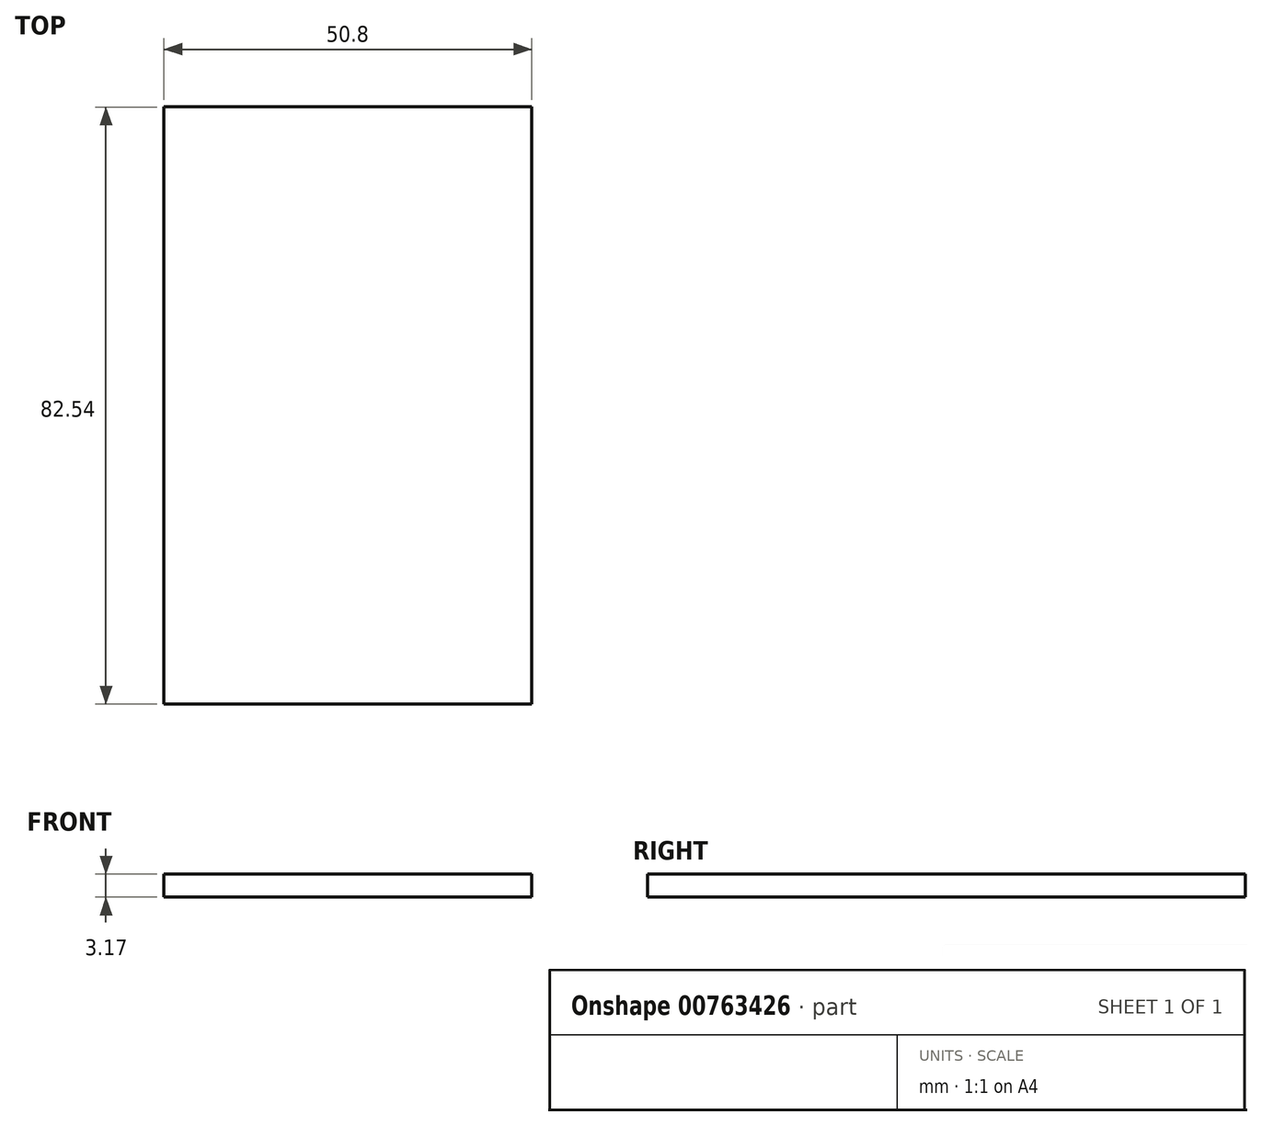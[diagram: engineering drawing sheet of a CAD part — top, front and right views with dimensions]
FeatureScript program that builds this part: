
annotation { "Feature Type Name" : "Feature", "Feature Type Description" : "" }
export const myFeature = defineFeature(function(context is Context, id is Id, definition is map)
    precondition{}
    {
        {
            var Q0;
            Q0=qCreatedBy(makeId("Top.planeOp"),FACE);
            var sketch = newSketch(context, id + "F0", { "sketchPlane" : qUnion([Q0])});
            skLineSegment(sketch, "E0.bottom", {"start": v(-25.4, 41.28) * mm, "end": v(25.4, 41.28) * mm});
            skLineSegment(sketch, "E0.top", {"start": v(-25.4, -41.28) * mm, "end": v(25.4, -41.28) * mm});
            skLineSegment(sketch, "E0.left", {"start": v(-25.4, 41.28) * mm, "end": v(-25.4, -41.28) * mm});
            skLineSegment(sketch, "E0.right", {"start": v(25.4, 41.28) * mm, "end": v(25.4, -41.28) * mm});
            skPoint(sketch, "E0.middle", {"position": v(0, 0) * mm});
            skSolve(sketch);
        }
        {
            var Q0;
            Q0=qCreatedBy(makeId("Top.planeOp"),FACE);
            var sketch = newSketch(context, id + "F1", { "sketchPlane" : qUnion([Q0])});
            skPoint(sketch, "E1", {"position": v(0, -22.23) * mm});
            skSolve(sketch);
        }
        {
            var Q0;
            Q0=qCreatedBy(makeId("Top.planeOp"),FACE);
            var sketch = newSketch(context, id + "F2", { "sketchPlane" : qUnion([Q0])});
            skSolve(sketch);
        }
        {
            var Q0;
            Q0 = qSketchRegion(id + "F2", true);
            var Q1;
            Q1=makeQuery(id+"F0.imprint","IMPRINT",FACE,{"disambiguationData":[TD([[makeQuery(id+"F0.imprint","IMPRINT",EDGE,{"derivedFrom":sQuery(id+"F0.wireOp",EDGE,"E0.bottom")}),-1.0]])]});
            extrude(context, id + "F3", {"entities" : qUnion([Q0, Q1]), "depth" : -3.17 * mm, "offsetDistance" : 25.4 * mm});
        }
        {
            var Q0;
            Q0=sQuery(id+"F1.wireOp",VERTEX,"E1");
            var Q1;
            Q1=makeQuery(id+"F3.opExtrude","SWEPT_BODY",BODY,{"disambiguationData":[OSD([sQuery(id+"F0.wireOp",EDGE,"E0.bottom"),sQuery(id+"F0.wireOp",EDGE,"E0.top"),sQuery(id+"F0.wireOp",EDGE,"E0.left"),sQuery(id+"F0.wireOp",EDGE,"E0.right")])]});
            hole(context, id + "F4", {"style" : HoleStyle.SIMPLE, "endStyle" : HoleEndStyle.THROUGH, "standardTappedOrClearance" : lookupTablePath({ "standard" : "ANSI", "fit" : "Normal (ASME)", "size" : "1", "type" : "Clearance" }), "standardBlindInLast" : lookupTablePath({ "fit" : "Free", "standard" : "ANSI", "size" : "1", "type" : "Clearance" }), "holeDiameter" : 26.2 * mm, "majorDiameter" : 15.88 * mm, "isTappedThrough" : true, "tappedDepth" : 12.7 * mm, "tapClearance" : 3, "locations" : qUnion([Q0]), "scope" : qUnion([Q1])});
        }
        {
            var Q0;
            Q0=makeQuery(id+"F3.opExtrude","SWEPT_FACE",FACE,{"disambiguationData":[OSD([sQuery(id+"F0.wireOp",EDGE,"E0.right")])]});
            extrude(context, id + "F5", {"entities" : qUnion([Q0]), "operationType" : NewBodyOperationType.ADD, "oppositeDirection" : true, "depth" : 50.8 * mm, "offsetDistance" : 25.4 * mm});
        }
    });
